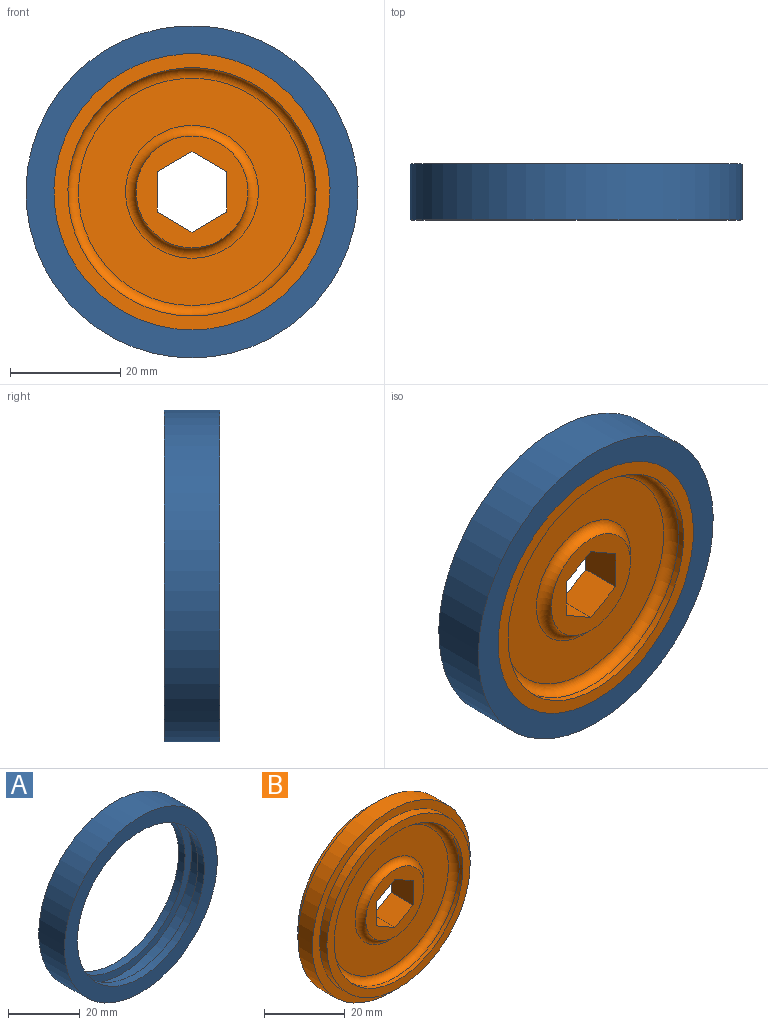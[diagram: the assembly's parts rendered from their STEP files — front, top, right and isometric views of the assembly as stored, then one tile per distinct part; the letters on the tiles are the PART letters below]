
ASSEMBLY  parts=2 mates=1
PART A: 8 faces, bbox 60.3x10.2x60.3 mm
  f0: cylinder r=30.16mm len=60.33mm, axis (0,-1,0), area 1925.5mm2, adj f1,f7
  f1: plane 60.33x60.33mm, normal (0,-1,0), area 881.7mm2, adj f0,f2
  f2: cylinder r=25.08mm len=50.17mm, axis (0,-1,0), area 400.3mm2, adj f1,f3
  f3: plane 55.25x55.25mm, normal (0,1,0), area 420.6mm2, adj f2,f4
  f4: cylinder r=27.62mm len=55.25mm, axis (0,-1,0), area 881.7mm2, adj f3,f5
  f5: plane 55.25x55.25mm, normal (0,-1,0), area 420.6mm2, adj f4,f6
  f6: cylinder r=25.08mm len=50.17mm, axis (0,-1,0), area 400.3mm2, adj f5,f7
  f7: plane 60.33x60.33mm, normal (0,1,0), area 881.7mm2, adj f0,f6
PART B: 23 faces, bbox 55.2x10.3x55.2 mm
  f0: plane 20.32x20.32mm, normal (0,-1,0), area 184.6mm2, adj f16,f17,f18,f19,f20,f21,f22
  f1: plane 20.32x20.32mm, normal (0,1,0), area 184.6mm2, adj f13,f17,f18,f19,f20,f21,f22
  f2: plane 41.28x41.28mm, normal (0,1,0), area 880.7mm2, adj f13,f14
  f3: cylinder r=22.54mm len=45.09mm, axis (0,-1,0), area 179.9mm2, adj f4,f14
  f4: plane 50.17x50.17mm, normal (0,1,0), area 380mm2, adj f3,f5
  f5: cylinder r=25.08mm len=50.17mm, axis (0,-1,0), area 400.3mm2, adj f4,f6
  f6: plane 55.25x55.25mm, normal (0,1,0), area 420.6mm2, adj f5,f7
  f7: cylinder r=27.62mm len=55.25mm, axis (0,-1,0), area 881.7mm2, adj f6,f8
  f8: plane 55.25x55.25mm, normal (0,-1,0), area 420.6mm2, adj f7,f9
  f9: cylinder r=25.08mm len=50.17mm, axis (0,-1,0), area 400.3mm2, adj f8,f10
  f10: plane 50.17x50.17mm, normal (0,-1,0), area 380mm2, adj f9,f11
  f11: cylinder r=22.54mm len=45.09mm, axis (0,-1,0), area 179.9mm2, adj f10,f15
  f12: plane 41.28x41.28mm, normal (0,-1,0), area 880.7mm2, adj f15,f16
  f13: torus R=12.06mm, axis (0,1,0), area 204mm2, adj f1,f2
  f14: torus R=20.64mm, axis (0,1,0), area 410.8mm2, adj f2,f3
  f15: torus R=20.64mm, axis (0,-1,0), area 410.8mm2, adj f11,f12
  f16: torus R=12.06mm, axis (0,-1,0), area 204mm2, adj f0,f12
  f17: plane 7.62x6.35mm, normal (-0.5,0,-0.87), area 55.9mm2, adj f0,f1,f18,f22
  f18: plane 7.62x6.35mm, normal (0.5,0,-0.87), area 55.9mm2, adj f0,f1,f17,f19
  f19: plane 7.62x7.33mm, normal (1,0,0), area 55.9mm2, adj f0,f1,f18,f20
  f20: plane 7.62x6.35mm, normal (0.5,0,0.87), area 55.9mm2, adj f0,f1,f19,f21
  f21: plane 7.62x6.35mm, normal (-0.5,0,0.87), area 55.9mm2, adj f0,f1,f20,f22
  f22: plane 7.62x7.33mm, normal (-1,0,0), area 55.9mm2, adj f0,f1,f17,f21
PLACE A at identity
PLACE B at identity
MATE fastened B.f3 <-> A.f0  axis (0,-1,0) through (0,-5.08,0)mm
